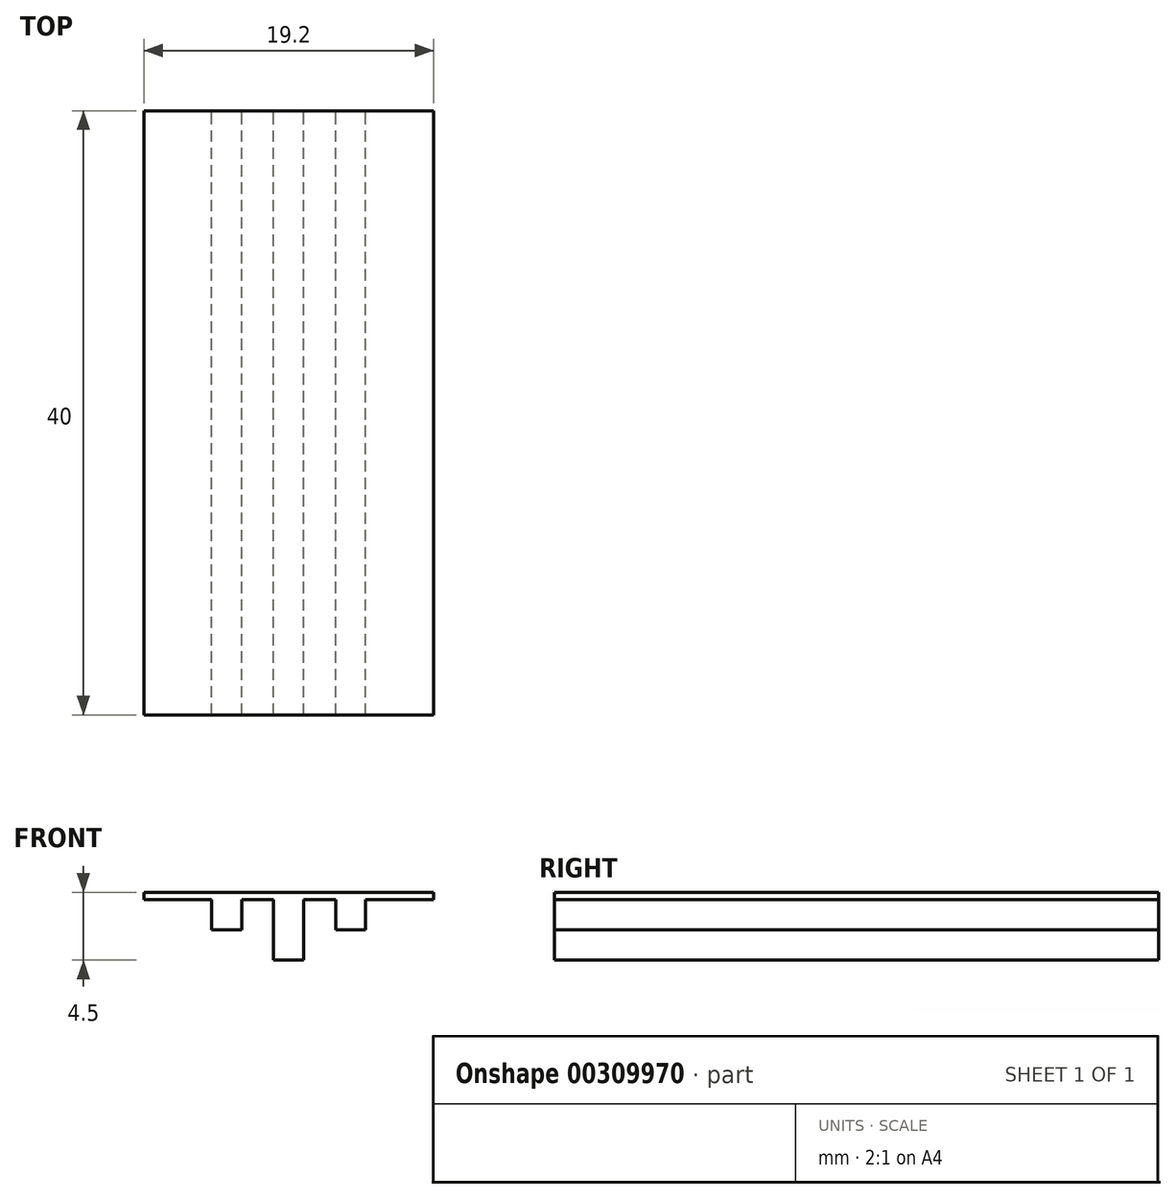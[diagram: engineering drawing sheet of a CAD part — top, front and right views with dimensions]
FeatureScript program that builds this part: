
annotation { "Feature Type Name" : "Feature", "Feature Type Description" : "" }
export const myFeature = defineFeature(function(context is Context, id is Id, definition is map)
    precondition{}
    {
        {
            var Q0;
            Q0=qCreatedBy(makeId("Front.planeOp"),FACE);
            var sketch = newSketch(context, id + "F0", { "sketchPlane" : qUnion([Q0])});
            skLineSegment(sketch, "E0", {"start": v(1, 0) * mm, "end": v(1, 4) * mm});
            skLineSegment(sketch, "E1", {"start": v(1, 4) * mm, "end": v(3.1, 4) * mm});
            skLineSegment(sketch, "E2", {"start": v(3.1, 4) * mm, "end": v(3.1, 2) * mm});
            skLineSegment(sketch, "E3", {"start": v(3.1, 2) * mm, "end": v(5.1, 2) * mm});
            skLineSegment(sketch, "E4", {"start": v(5.1, 2) * mm, "end": v(5.1, 4) * mm});
            skLineSegment(sketch, "E5", {"start": v(5.1, 4) * mm, "end": v(9.6, 4) * mm});
            skLineSegment(sketch, "E6", {"start": v(9.6, 4) * mm, "end": v(9.6, 4.5) * mm});
            skLineSegment(sketch, "E7", {"start": v(1, 2) * mm, "end": v(1, 4) * mm});
            skLineSegment(sketch, "E8", {"start": v(1, 0) * mm, "end": v(0, 0) * mm});
            skLineSegment(sketch, "E9.MirrorCS", {"start": v(-1, 0) * mm, "end": v(0, 0) * mm});
            skLineSegment(sketch, "E10.MirrorCS", {"start": v(-1, 0) * mm, "end": v(-1, 4) * mm});
            skLineSegment(sketch, "E11.MirrorCS", {"start": v(-1, 4) * mm, "end": v(-3.1, 4) * mm});
            skLineSegment(sketch, "E12.MirrorCS", {"start": v(-3.1, 4) * mm, "end": v(-3.1, 2) * mm});
            skLineSegment(sketch, "E13.MirrorCS", {"start": v(-3.1, 2) * mm, "end": v(-5.1, 2) * mm});
            skLineSegment(sketch, "E14.MirrorCS", {"start": v(-5.1, 2) * mm, "end": v(-5.1, 4) * mm});
            skLineSegment(sketch, "E15.MirrorCS", {"start": v(-5.1, 4) * mm, "end": v(-9.6, 4) * mm});
            skLineSegment(sketch, "E16.MirrorCS", {"start": v(-9.6, 4) * mm, "end": v(-9.6, 4.5) * mm});
            skLineSegment(sketch, "E17", {"start": v(-9.6, 4.5) * mm, "end": v(9.6, 4.5) * mm});
            skSolve(sketch);
        }
        {
            var Q0;
            Q0 = qSketchRegion(id + "F0", true);
            extrude(context, id + "F1", {"entities" : qUnion([Q0]), "depth" : 40 * mm});
        }
    });
